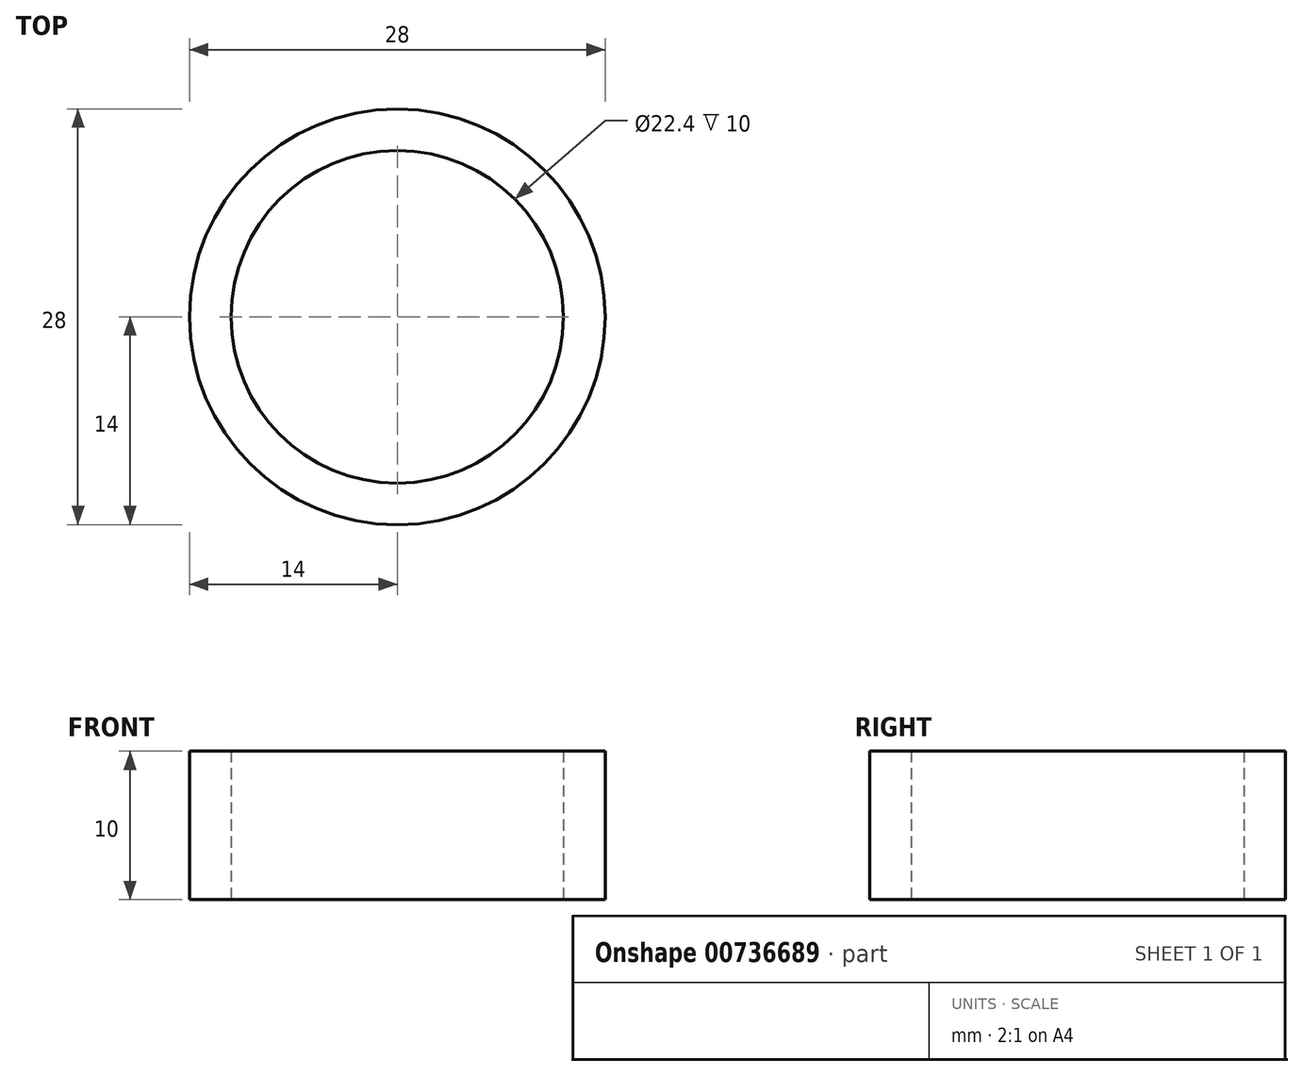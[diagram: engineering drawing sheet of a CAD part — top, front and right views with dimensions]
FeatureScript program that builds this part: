
annotation { "Feature Type Name" : "Feature", "Feature Type Description" : "" }
export const myFeature = defineFeature(function(context is Context, id is Id, definition is map)
    precondition{}
    {
        {
            var Q0;
            Q0=qCreatedBy(makeId("Top.planeOp"),FACE);
            var sketch = newSketch(context, id + "F0", { "sketchPlane" : qUnion([Q0])});
            skCircle(sketch, "E0", {"center": v(0, 0) * mm, "radius": 11.2 * mm});
            skCircle(sketch, "E1", {"center": v(0, 0) * mm, "radius": 14 * mm});
            skSolve(sketch);
        }
        {
            var Q0;
            Q0 = qSketchRegion(id + "F0", true);
            extrude(context, id + "F1", {"entities" : qUnion([Q0]), "depth" : 10 * mm, "offsetDistance" : 25 * mm});
        }
    });
